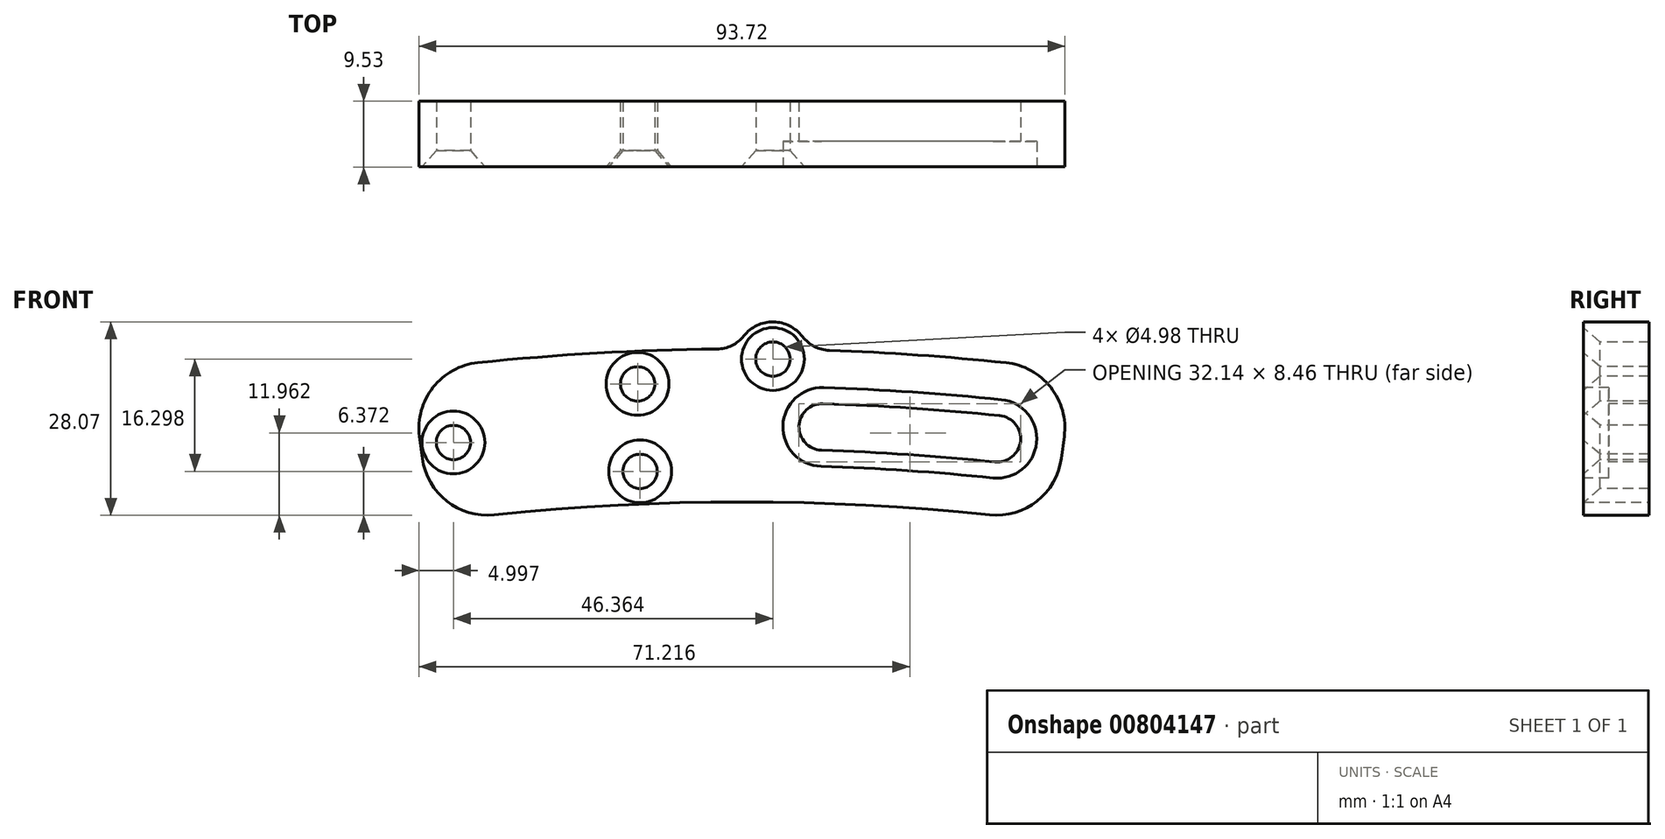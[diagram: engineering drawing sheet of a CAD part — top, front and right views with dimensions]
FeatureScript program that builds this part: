
annotation { "Feature Type Name" : "Feature", "Feature Type Description" : "" }
export const myFeature = defineFeature(function(context is Context, id is Id, definition is map)
    precondition{}
    {
        {
            var Q0;
            Q0=qCreatedBy(makeId("Front.planeOp"),FACE);
            var sketch = newSketch(context, id + "F0", { "sketchPlane" : qUnion([Q0])});
            skLineSegment(sketch, "E0", {"start": v(0, 0) * mm, "end": v(0, -330.2) * mm, "construction": true});
            skLineSegment(sketch, "E1", {"start": v(0, -330.2) * mm, "end": v(-45.14, 12.66) * mm, "construction": true});
            skLineSegment(sketch, "E2", {"start": v(0, -330.2) * mm, "end": v(45.14, 12.66) * mm, "construction": true});
            skArc(sketch, "E3", {"start": v(-48.04, 34.7) * mm, "mid": v(0, 37.85) * mm, "end": v(48.04, 34.7) * mm});
            skArc(sketch, "E4.0", {"start": v(-45.14, 12.66) * mm, "mid": v(0, 15.62) * mm, "end": v(45.14, 12.66) * mm});
            skLineSegment(sketch, "E5", {"start": v(-48.04, 34.7) * mm, "end": v(-45.14, 12.66) * mm});
            skLineSegment(sketch, "E6", {"start": v(45.14, 12.66) * mm, "end": v(48.04, 34.7) * mm});
            skArc(sketch, "E7.0", {"start": v(-46.59, 23.68) * mm, "mid": v(0, 26.7) * mm, "end": v(46.59, 23.68) * mm, "construction": true});
            skPoint(sketch, "E8", {"position": v(-46.59, 23.68) * mm});
            skCircle(sketch, "E9", {"center": v(-41.86, 24.26) * mm, "radius": 4.76 * mm, "construction": true});
            skCircle(sketch, "E10", {"center": v(-15.13, 32.77) * mm, "radius": 4.76 * mm, "construction": true});
            skCircle(sketch, "E11", {"center": v(-14.77, 20.07) * mm, "radius": 4.76 * mm, "construction": true});
            skLineSegment(sketch, "E12", {"start": v(-10.5, 37.7) * mm, "end": v(-9.88, 15.48) * mm, "construction": true});
            skPoint(sketch, "E13", {"position": v(-10.2, 26.59) * mm});
            skPoint(sketch, "E14", {"position": v(46.59, 23.68) * mm});
            skSolve(sketch);
        }
        {
            var Q0;
            Q0 = qSketchRegion(id + "F0", true);
            extrude(context, id + "F1", {"entities" : qUnion([Q0]), "depth" : 9.52 * mm, "offsetDistance" : 25.4 * mm});
        }
        {
            var Q0;
            Q0=makeQuery(id+"F1.opExtrude","CAP_FACE",FACE,{"disambiguationData":[OSD([sQuery(id+"F0.wireOp",EDGE,"E3"),sQuery(id+"F0.wireOp",EDGE,"E4.0"),sQuery(id+"F0.wireOp",EDGE,"E5"),sQuery(id+"F0.wireOp",EDGE,"E6")])],"isStart":false});
            var sketch = newSketch(context, id + "F2", { "sketchPlane" : qUnion([Q0])});
            skCircle(sketch, "E15.0", {"center": v(-15.13, 32.77) * mm, "radius": 4.76 * mm, "construction": true});
            skCircle(sketch, "E15.1", {"center": v(-14.77, 20.07) * mm, "radius": 4.76 * mm, "construction": true});
            skCircle(sketch, "E15.2", {"center": v(-41.86, 24.26) * mm, "radius": 4.76 * mm, "construction": true});
            skSolve(sketch);
        }
        {
            var Q0;
            Q0=sQuery(id+"F2.wireOp",VERTEX,"E15.0.center");
            var Q1;
            Q1=sQuery(id+"F2.wireOp",VERTEX,"E15.1.center");
            var Q2;
            Q2=sQuery(id+"F2.wireOp",VERTEX,"E15.2.center");
            var Q3;
            Q3=makeQuery(id+"F1.opExtrude","SWEPT_BODY",BODY,{"disambiguationData":[OSD([sQuery(id+"F0.wireOp",EDGE,"E3"),sQuery(id+"F0.wireOp",EDGE,"E4.0"),sQuery(id+"F0.wireOp",EDGE,"E5"),sQuery(id+"F0.wireOp",EDGE,"E6")])]});
            hole(context, id + "F3", {"style" : HoleStyle.C_SINK, "endStyle" : HoleEndStyle.THROUGH, "standardTappedOrClearance" : lookupTablePath({ "fit" : "Normal (ASME)", "standard" : "ANSI", "size" : "#8", "type" : "Clearance" }), "standardBlindInLast" : lookupTablePath({ "fit" : "Normal", "standard" : "ANSI", "size" : "#8", "type" : "Clearance" }), "holeDiameter" : 4.98 * mm, "cSinkDiameter" : 9.12 * mm, "cSinkAngle" : 82 * degree, "majorDiameter" : 6.35 * mm, "tappedDepth" : 9.52 * mm, "tapClearance" : 3, "startFromSketch" : true, "locations" : qUnion([Q0, Q1, Q2]), "scope" : qUnion([Q3])});
        }
        {
            var Q0;
            Q0=makeQuery(id+"F1.opExtrude","CAP_FACE",FACE,{"disambiguationData":[OSD([sQuery(id+"F0.wireOp",EDGE,"E3"),sQuery(id+"F0.wireOp",EDGE,"E4.0"),sQuery(id+"F0.wireOp",EDGE,"E5"),sQuery(id+"F0.wireOp",EDGE,"E6")])],"isStart":false});
            var sketch = newSketch(context, id + "F4", { "sketchPlane" : qUnion([Q0])});
            skArc(sketch, "E16.0", {"start": v(11.66, 26.52) * mm, "mid": v(24.38, 25.88) * mm, "end": v(37.06, 24.8) * mm, "construction": true});
            skPoint(sketch, "E17", {"position": v(11.66, 26.52) * mm});
            skPoint(sketch, "E18", {"position": v(37.06, 24.8) * mm});
            skLineSegment(sketch, "E19", {"start": v(11.66, 26.52) * mm, "end": v(11.3, 15.44) * mm, "construction": true});
            skLineSegment(sketch, "E20", {"start": v(37.06, 24.8) * mm, "end": v(35.92, 13.75) * mm, "construction": true});
            skPoint(sketch, "E21.orphan", {"position": v(-46.59, 23.68) * mm});
            skPoint(sketch, "E22.orphan", {"position": v(46.59, 23.68) * mm});
            skArc(sketch, "E23.0.startCap", {"start": v(11.55, 23.14) * mm, "mid": v(8.29, 26.62) * mm, "end": v(11.77, 29.9) * mm});
            skArc(sketch, "E23.0.endCap", {"start": v(37.41, 28.15) * mm, "mid": v(40.42, 24.45) * mm, "end": v(36.72, 21.43) * mm});
            skArc(sketch, "E23.0.left", {"start": v(11.77, 29.9) * mm, "mid": v(24.6, 29.25) * mm, "end": v(37.41, 28.15) * mm});
            skArc(sketch, "E23.0.right", {"start": v(11.55, 23.14) * mm, "mid": v(24.15, 22.5) * mm, "end": v(36.72, 21.43) * mm});
            skSolve(sketch);
        }
        {
            var Q0;
            Q0 = qSketchRegion(id + "F4", true);
            extrude(context, id + "F5", {"entities" : qUnion([Q0]), "operationType" : NewBodyOperationType.REMOVE, "endBound" : BoundingType.THROUGH_ALL, "oppositeDirection" : true, "depth" : 25.4 * mm, "offsetDistance" : 25.4 * mm});
        }
        {
            var Q0;
            Q0=makeQuery(id+"F1.opExtrude","CAP_FACE",FACE,{"disambiguationData":[OSD([sQuery(id+"F0.wireOp",EDGE,"E3"),sQuery(id+"F0.wireOp",EDGE,"E4.0"),sQuery(id+"F0.wireOp",EDGE,"E5"),sQuery(id+"F0.wireOp",EDGE,"E6")])],"isStart":false});
            var Q1;
            Q1=makeQuery(id+"F0.imprint","IMPRINT",FACE,{"disambiguationData":[TD([[makeQuery(id+"F0.imprint","IMPRINT",EDGE,{"derivedFrom":sQuery(id+"F0.wireOp",EDGE,"E3")}),-1.0]])]});
            var sketch = newSketch(context, id + "F6", { "sketchPlane" : qUnion([Q0, Q1])});
            skArc(sketch, "E24.0", {"start": v(11.55, 23.14) * mm, "mid": v(24.15, 22.5) * mm, "end": v(36.72, 21.43) * mm});
            skArc(sketch, "E25.0", {"start": v(37.41, 28.15) * mm, "mid": v(40.42, 24.45) * mm, "end": v(36.72, 21.43) * mm});
            skArc(sketch, "E25.1", {"start": v(11.77, 29.9) * mm, "mid": v(24.6, 29.25) * mm, "end": v(37.41, 28.15) * mm});
            skArc(sketch, "E25.2", {"start": v(11.55, 23.14) * mm, "mid": v(8.29, 26.62) * mm, "end": v(11.77, 29.9) * mm});
            skArc(sketch, "E26.0", {"start": v(11.48, 20.8) * mm, "mid": v(24, 20.18) * mm, "end": v(36.48, 19.1) * mm});
            skArc(sketch, "E26.1", {"start": v(11.48, 20.8) * mm, "mid": v(5.95, 26.7) * mm, "end": v(11.85, 32.23) * mm});
            skArc(sketch, "E26.2", {"start": v(11.85, 32.23) * mm, "mid": v(24.77, 31.58) * mm, "end": v(37.65, 30.48) * mm});
            skArc(sketch, "E26.3", {"start": v(37.65, 30.48) * mm, "mid": v(42.75, 24.2) * mm, "end": v(36.48, 19.1) * mm});
            skSolve(sketch);
        }
        {
            var Q0;
            Q0 = qSketchRegion(id + "F6", true);
            extrude(context, id + "F7", {"entities" : qUnion([Q0]), "operationType" : NewBodyOperationType.REMOVE, "oppositeDirection" : true, "depth" : 3.68 * mm, "offsetDistance" : 25.4 * mm});
        }
        {
            var Q0;
            Q0=makeQuery(id+"F6.imprint","IMPRINT",FACE,{"disambiguationData":[TD([[makeQuery(id+"F6.imprint","IMPRINT",EDGE,{"derivedFrom":sQuery(id+"F6.wireOp",EDGE,"E26.0")}),-1.0]])]});
            var sketch = newSketch(context, id + "F8", { "sketchPlane" : qUnion([Q0])});
            skArc(sketch, "E27.0", {"start": v(-48.04, 34.7) * mm, "mid": v(0, 37.85) * mm, "end": v(48.04, 34.7) * mm, "construction": true});
            skLineSegment(sketch, "E28", {"start": v(4.52, 37.82) * mm, "end": v(4.38, 26.68) * mm, "construction": true});
            skArc(sketch, "E29.0", {"start": v(-46.59, 23.68) * mm, "mid": v(0, 26.7) * mm, "end": v(46.59, 23.68) * mm, "construction": true});
            skPoint(sketch, "E30", {"position": v(4.5, 36.37) * mm});
            skCircle(sketch, "E31", {"center": v(4.5, 36.37) * mm, "radius": 5.4 * mm});
            skSolve(sketch);
        }
        {
            var Q0;
            Q0 = qSketchRegion(id + "F8", true);
            var Q1;
            Q1=makeQuery(id+"F1.opExtrude","CAP_FACE",FACE,{"disambiguationData":[OSD([sQuery(id+"F0.wireOp",EDGE,"E3"),sQuery(id+"F0.wireOp",EDGE,"E4.0"),sQuery(id+"F0.wireOp",EDGE,"E5"),sQuery(id+"F0.wireOp",EDGE,"E6")])],"isStart":true});
            extrude(context, id + "F9", {"entities" : qUnion([Q0]), "operationType" : NewBodyOperationType.ADD, "endBound" : BoundingType.UP_TO_SURFACE, "oppositeDirection" : true, "depth" : 25.4 * mm, "endBoundEntityFace" : qUnion([Q1]), "offsetDistance" : 25.4 * mm});
        }
        {
            var Q0;
            Q0=sQuery(id+"F8.wireOp",VERTEX,"E30");
            var Q1;
            Q1=makeQuery(id+"F1.opExtrude","SWEPT_BODY",BODY,{"disambiguationData":[OSD([sQuery(id+"F0.wireOp",EDGE,"E3"),sQuery(id+"F0.wireOp",EDGE,"E4.0"),sQuery(id+"F0.wireOp",EDGE,"E5"),sQuery(id+"F0.wireOp",EDGE,"E6")])]});
            hole(context, id + "F10", {"style" : HoleStyle.C_SINK, "endStyle" : HoleEndStyle.THROUGH, "standardTappedOrClearance" : lookupTablePath({ "fit" : "Normal (ASME)", "standard" : "ANSI", "size" : "#8", "type" : "Clearance" }), "standardBlindInLast" : lookupTablePath({ "fit" : "Normal", "standard" : "ANSI", "size" : "#8", "type" : "Clearance" }), "holeDiameter" : 4.98 * mm, "cSinkDiameter" : 9.12 * mm, "cSinkAngle" : 82 * degree, "majorDiameter" : 6.35 * mm, "tappedDepth" : 9.52 * mm, "tapClearance" : 3, "startFromSketch" : true, "locations" : qUnion([Q0]), "scope" : qUnion([Q1])});
        }
        {
            var Q0;
            Q0=makeQuery(id+"F1.opExtrude","SWEPT_EDGE",EDGE,{"disambiguationData":[OSD([sQuery(id+"F0.wireOp",EDGE,"E3"),sQuery(id+"F0.wireOp",EDGE,"E5")])]});
            var Q1;
            Q1=makeQuery(id+"F1.opExtrude","SWEPT_EDGE",EDGE,{"disambiguationData":[OSD([sQuery(id+"F0.wireOp",EDGE,"E4.0"),sQuery(id+"F0.wireOp",EDGE,"E5")])]});
            var Q2;
            Q2=makeQuery(id+"F1.opExtrude","SWEPT_EDGE",EDGE,{"disambiguationData":[OSD([sQuery(id+"F0.wireOp",EDGE,"E4.0"),sQuery(id+"F0.wireOp",EDGE,"E6")])]});
            var Q3;
            Q3=makeQuery(id+"F1.opExtrude","SWEPT_EDGE",EDGE,{"disambiguationData":[OSD([sQuery(id+"F0.wireOp",EDGE,"E3"),sQuery(id+"F0.wireOp",EDGE,"E6")])]});
            fillet(context, id + "F11", {"entities" : qUnion([Q0, Q1, Q2, Q3]), "radius" : 9.52 * mm, "tangentPropagation" : true, "allowEdgeOverflow" : false});
        }
        {
            var Q0;
            Q0=makeQuery(id+"F9.boolean.opBoolean","INTERSECT",EDGE,{"disambiguationData":[OD(1.0)],"derivedFrom":[makeQuery(id+"F1.opExtrude","SWEPT_FACE",FACE,{"disambiguationData":[OSD([sQuery(id+"F0.wireOp",EDGE,"E3")])]}),makeQuery(id+"F9.opExtrude","SWEPT_FACE",FACE,{"disambiguationData":[OSD([sQuery(id+"F8.wireOp",EDGE,"E31")])]})]});
            var Q1;
            Q1=makeQuery(id+"F9.boolean.opBoolean","INTERSECT",EDGE,{"disambiguationData":[OD(0.0)],"derivedFrom":[makeQuery(id+"F1.opExtrude","SWEPT_FACE",FACE,{"disambiguationData":[OSD([sQuery(id+"F0.wireOp",EDGE,"E3")])]}),makeQuery(id+"F9.opExtrude","SWEPT_FACE",FACE,{"disambiguationData":[OSD([sQuery(id+"F8.wireOp",EDGE,"E31")])]})]});
            fillet(context, id + "F12", {"entities" : qUnion([Q0, Q1]), "radius" : 5.08 * mm, "tangentPropagation" : true, "allowEdgeOverflow" : false});
        }
    });
